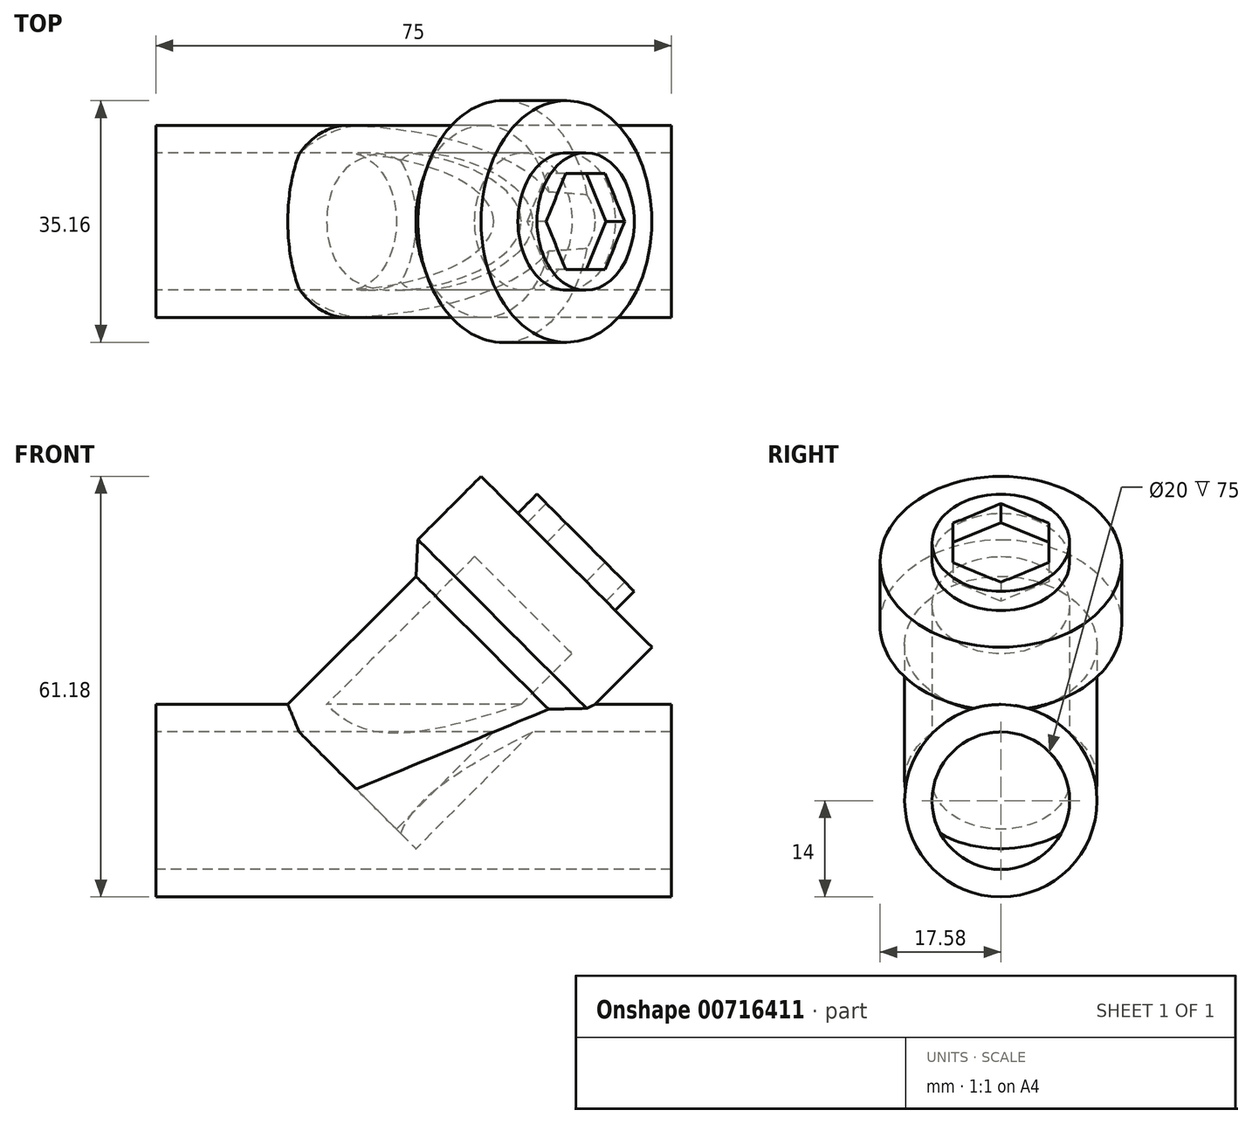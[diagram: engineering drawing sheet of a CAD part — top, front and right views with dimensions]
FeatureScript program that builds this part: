
annotation { "Feature Type Name" : "Feature", "Feature Type Description" : "" }
export const myFeature = defineFeature(function(context is Context, id is Id, definition is map)
    precondition{}
    {
        {
            var Q0;
            Q0=qCreatedBy(makeId("Top.planeOp"),FACE);
            var sketch = newSketch(context, id + "F0", { "sketchPlane" : qUnion([Q0])});
            skLineSegment(sketch, "E0", {"start": v(-59.15, 0) * mm, "end": v(57.24, 0) * mm, "construction": true});
            skLineSegment(sketch, "E1.bottom", {"start": v(-25, 14) * mm, "end": v(50, 14) * mm});
            skLineSegment(sketch, "E1.top", {"start": v(-25, 10) * mm, "end": v(50, 10) * mm});
            skLineSegment(sketch, "E1.left", {"start": v(-25, 14) * mm, "end": v(-25, 10) * mm});
            skLineSegment(sketch, "E1.right", {"start": v(50, 14) * mm, "end": v(50, 10) * mm});
            skSolve(sketch);
        }
        {
            var Q0;
            Q0 = qSketchRegion(id + "F0", true);
            var Q1;
            Q1=sQuery(id+"F0.wireOp",EDGE,"E0");
            revolve(context, id + "F1", {"surfaceOperationType" : NewSurfaceOperationType.NEW, "entities" : qUnion([Q0]), "axis" : qUnion([Q1]), "revolveType" : RevolveType.FULL});
        }
        {
            var Q0;
            Q0=qCreatedBy(makeId("Front.planeOp"),FACE);
            var sketch = newSketch(context, id + "F2", { "sketchPlane" : qUnion([Q0])});
            skLineSegment(sketch, "E2", {"start": v(0, 0) * mm, "end": v(37.41, 37.41) * mm, "construction": true});
            skLineSegment(sketch, "E3", {"start": v(-4.14, 10) * mm, "end": v(21.39, 35.53) * mm});
            skLineSegment(sketch, "E4", {"start": v(27.68, 41.82) * mm, "end": v(22.32, 47.18) * mm});
            skLineSegment(sketch, "E5", {"start": v(22.32, 47.18) * mm, "end": v(13.12, 37.99) * mm});
            skLineSegment(sketch, "E6", {"start": v(13.12, 37.99) * mm, "end": v(12.83, 32.63) * mm});
            skLineSegment(sketch, "E7", {"start": v(12.83, 32.63) * mm, "end": v(-6.97, 12.83) * mm});
            skLineSegment(sketch, "E8", {"start": v(-6.97, 12.83) * mm, "end": v(-4.14, 10) * mm});
            skLineSegment(sketch, "E9", {"start": v(27.68, 41.82) * mm, "end": v(30.46, 44.6) * mm});
            skLineSegment(sketch, "E10", {"start": v(30.46, 44.6) * mm, "end": v(37.41, 37.41) * mm});
            skLineSegment(sketch, "E11", {"start": v(21.39, 35.53) * mm, "end": v(28.46, 28.46) * mm});
            skLineSegment(sketch, "E12", {"start": v(28.46, 28.46) * mm, "end": v(37.41, 37.41) * mm});
            skSolve(sketch);
        }
        {
            var Q0;
            Q0 = qSketchRegion(id + "F2", true);
            var Q1;
            Q1=sQuery(id+"F2.wireOp",EDGE,"E2");
            revolve(context, id + "F3", {"operationType" : NewBodyOperationType.ADD, "surfaceOperationType" : NewSurfaceOperationType.NEW, "entities" : qUnion([Q0]), "axis" : qUnion([Q1]), "revolveType" : RevolveType.FULL});
        }
        {
            var Q0;
            Q0=makeQuery(id+"F3.opRevolve","SWEPT_FACE",FACE,{"disambiguationData":[OSD([sQuery(id+"F2.wireOp",EDGE,"E4")])]});
            var sketch = newSketch(context, id + "F4", { "sketchPlane" : qUnion([Q0])});
            skCircle(sketch, "E13.cCircle", {"center": v(0, 0) * mm, "radius": 7 * mm, "construction": true});
            skLineSegment(sketch, "E13.0", {"start": v(7, 4.04) * mm, "end": v(7, -4.04) * mm});
            skLineSegment(sketch, "E13.1", {"start": v(7, -4.04) * mm, "end": v(0, -8.08) * mm});
            skLineSegment(sketch, "E13.2", {"start": v(0, -8.08) * mm, "end": v(-7, -4.04) * mm});
            skLineSegment(sketch, "E13.3", {"start": v(-7, -4.04) * mm, "end": v(-7, 4.04) * mm});
            skLineSegment(sketch, "E13.4", {"start": v(-7, 4.04) * mm, "end": v(0, 8.08) * mm});
            skLineSegment(sketch, "E13.5", {"start": v(0, 8.08) * mm, "end": v(7, 4.04) * mm});
            skPoint(sketch, "E13.0.midPoint", {"position": v(7, 0) * mm});
            skSolve(sketch);
        }
        {
            var Q0;
            Q0 = qSketchRegion(id + "F4", true);
            extrude(context, id + "F5", {"entities" : qUnion([Q0]), "operationType" : NewBodyOperationType.REMOVE, "depth" : 25 * mm, "offsetDistance" : 25 * mm});
        }
    });
